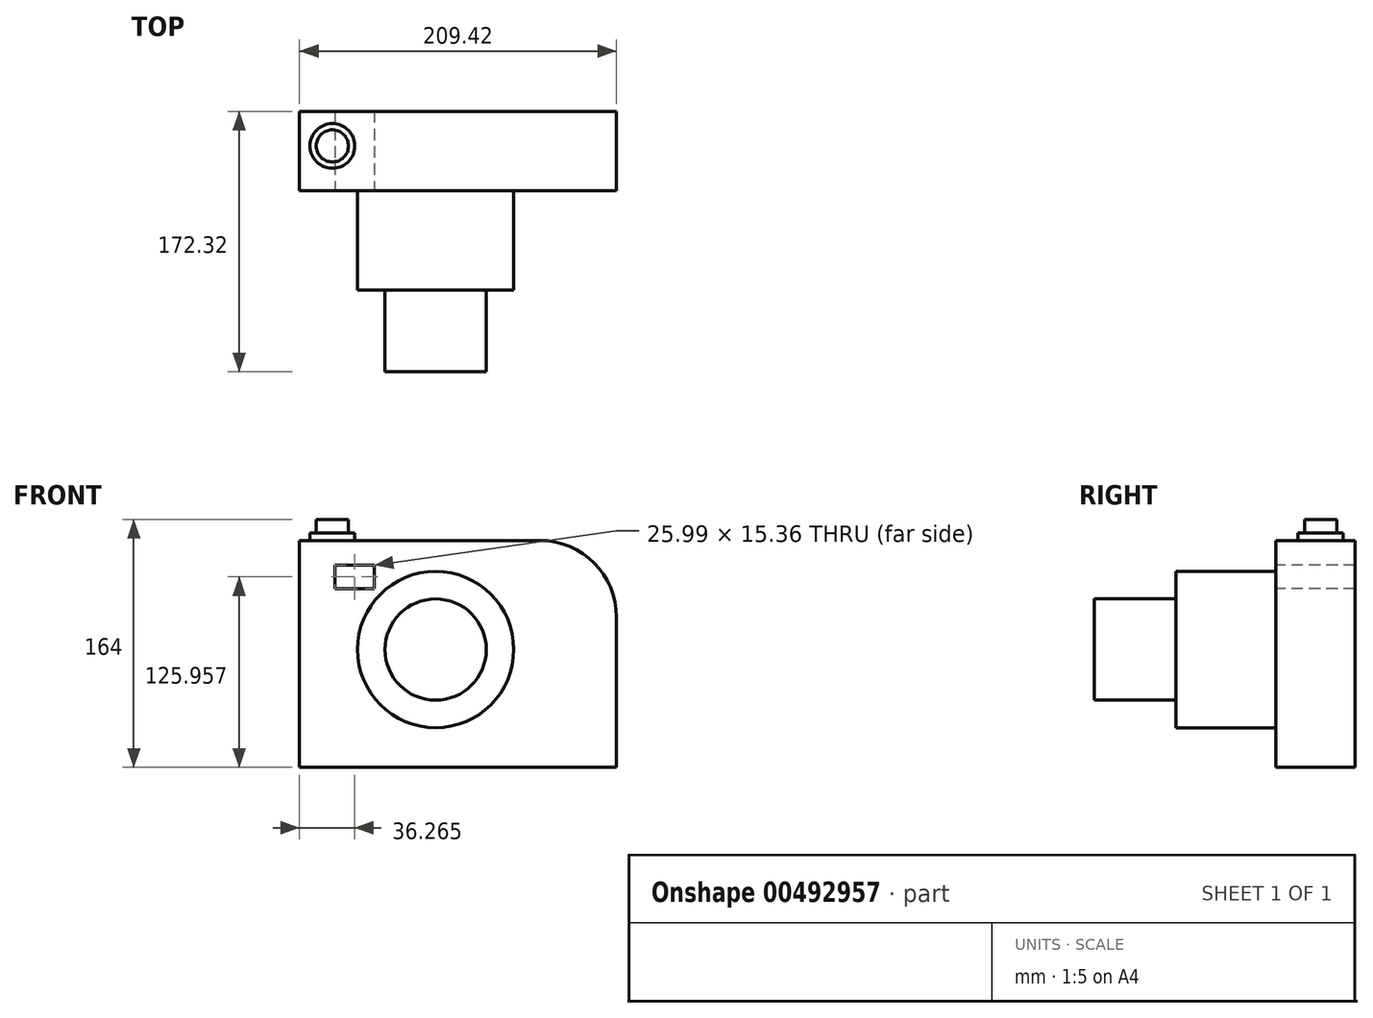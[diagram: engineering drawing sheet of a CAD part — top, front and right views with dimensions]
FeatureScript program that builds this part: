
annotation { "Feature Type Name" : "Feature", "Feature Type Description" : "" }
export const myFeature = defineFeature(function(context is Context, id is Id, definition is map)
    precondition{}
    {
        {
            var Q0;
            Q0=qCreatedBy(makeId("Top.planeOp"),FACE);
            var sketch = newSketch(context, id + "F0", { "sketchPlane" : qUnion([Q0])});
            skLineSegment(sketch, "E0.bottom", {"start": v(-159.83, -84.87) * mm, "end": v(49.6, -84.87) * mm});
            skLineSegment(sketch, "E0.top", {"start": v(-159.83, -32.55) * mm, "end": v(49.6, -32.55) * mm});
            skLineSegment(sketch, "E0.left", {"start": v(-159.83, -84.87) * mm, "end": v(-159.83, -32.55) * mm});
            skLineSegment(sketch, "E0.right", {"start": v(49.6, -84.87) * mm, "end": v(49.6, -32.55) * mm});
            skSolve(sketch);
        }
        {
            var Q0;
            Q0 = qSketchRegion(id + "F0", true);
            extrude(context, id + "F1", {"entities" : qUnion([Q0]), "depth" : 150 * mm});
        }
        {
            var Q0;
            Q0=makeQuery(id+"F1.opExtrude","CAP_EDGE",EDGE,{"disambiguationData":[OSD([sQuery(id+"F0.wireOp",EDGE,"E0.right")])],"isStart":false});
            fillet(context, id + "F2", {"entities" : qUnion([Q0]), "radius" : 50.7 * mm, "tangentPropagation" : true, "allowEdgeOverflow" : false});
        }
        {
            var Q0;
            Q0=makeQuery(id+"F1.opExtrude","SWEPT_FACE",FACE,{"disambiguationData":[OSD([sQuery(id+"F0.wireOp",EDGE,"E0.bottom")])]});
            var sketch = newSketch(context, id + "F3", { "sketchPlane" : qUnion([Q0])});
            skCircle(sketch, "E1", {"center": v(-69.93, 77.87) * mm, "radius": 51.66 * mm});
            skSolve(sketch);
        }
        {
            var Q0;
            Q0 = qSketchRegion(id + "F3", true);
            extrude(context, id + "F4", {"entities" : qUnion([Q0]), "operationType" : NewBodyOperationType.ADD, "depth" : 66 * mm});
        }
        {
            var Q0;
            Q0=makeQuery(id+"F4.opExtrude","CAP_FACE",FACE,{"disambiguationData":[OSD([sQuery(id+"F3.wireOp",EDGE,"E1")])],"isStart":false});
            var sketch = newSketch(context, id + "F5", { "sketchPlane" : qUnion([Q0])});
            skCircle(sketch, "E2", {"center": v(-69.93, 77.87) * mm, "radius": 33.47 * mm});
            skSolve(sketch);
        }
        {
            var Q0;
            Q0 = qSketchRegion(id + "F5", true);
            extrude(context, id + "F6", {"entities" : qUnion([Q0]), "operationType" : NewBodyOperationType.ADD, "depth" : 54 * mm});
        }
        {
            var Q0;
            Q0=makeQuery(id+"F1.opExtrude","CAP_FACE",FACE,{"disambiguationData":[OSD([sQuery(id+"F0.wireOp",EDGE,"E0.bottom"),sQuery(id+"F0.wireOp",EDGE,"E0.top"),sQuery(id+"F0.wireOp",EDGE,"E0.left"),sQuery(id+"F0.wireOp",EDGE,"E0.right")])],"isStart":false});
            var sketch = newSketch(context, id + "F7", { "sketchPlane" : qUnion([Q0])});
            skCircle(sketch, "E3", {"center": v(-138.17, -55.4) * mm, "radius": 14.8 * mm});
            skSolve(sketch);
        }
        {
            var Q0;
            Q0 = qSketchRegion(id + "F7", true);
            extrude(context, id + "F8", {"entities" : qUnion([Q0]), "operationType" : NewBodyOperationType.ADD, "depth" : 5 * mm});
        }
        {
            var Q0;
            Q0=makeQuery(id+"F8.opExtrude","CAP_FACE",FACE,{"disambiguationData":[OSD([sQuery(id+"F7.wireOp",EDGE,"E3")])],"isStart":false});
            var sketch = newSketch(context, id + "F9", { "sketchPlane" : qUnion([Q0])});
            skCircle(sketch, "E4", {"center": v(-138.17, -55.4) * mm, "radius": 10.62 * mm});
            skSolve(sketch);
        }
        {
            var Q0;
            Q0 = qSketchRegion(id + "F9", true);
            extrude(context, id + "F10", {"entities" : qUnion([Q0]), "operationType" : NewBodyOperationType.ADD, "depth" : 9 * mm});
        }
        {
            var Q0;
            Q0=makeQuery(id+"F1.opExtrude","SWEPT_FACE",FACE,{"disambiguationData":[OSD([sQuery(id+"F0.wireOp",EDGE,"E0.bottom")])]});
            var sketch = newSketch(context, id + "F11", { "sketchPlane" : qUnion([Q0])});
            skLineSegment(sketch, "E5.bottom", {"start": v(-152.36, 134.7) * mm, "end": v(-118.32, 134.7) * mm});
            skLineSegment(sketch, "E5.top", {"start": v(-152.36, 117.7) * mm, "end": v(-118.32, 117.7) * mm});
            skLineSegment(sketch, "E5.left", {"start": v(-152.36, 134.7) * mm, "end": v(-152.36, 117.7) * mm});
            skLineSegment(sketch, "E5.right", {"start": v(-118.32, 134.7) * mm, "end": v(-118.32, 117.7) * mm});
            skSolve(sketch);
        }
        {
            var Q0;
            Q0 = qSketchRegion(id + "F11", true);
            extrude(context, id + "F12", {"entities" : qUnion([Q0]), "operationType" : NewBodyOperationType.ADD, "oppositeDirection" : true, "depth" : 43 * mm});
        }
        {
            var Q0;
            Q0=makeQuery(id+"F1.opExtrude","SWEPT_FACE",FACE,{"disambiguationData":[OSD([sQuery(id+"F0.wireOp",EDGE,"E0.bottom")])]});
            var sketch = newSketch(context, id + "F13", { "sketchPlane" : qUnion([Q0])});
            skLineSegment(sketch, "E6.bottom", {"start": v(-136.56, 133.64) * mm, "end": v(-110.57, 133.64) * mm});
            skLineSegment(sketch, "E6.top", {"start": v(-136.56, 118.28) * mm, "end": v(-110.57, 118.28) * mm});
            skLineSegment(sketch, "E6.left", {"start": v(-136.56, 133.64) * mm, "end": v(-136.56, 118.28) * mm});
            skLineSegment(sketch, "E6.right", {"start": v(-110.57, 133.64) * mm, "end": v(-110.57, 118.28) * mm});
            skSolve(sketch);
        }
        {
            var Q0;
            Q0 = qSketchRegion(id + "F13", true);
            extrude(context, id + "F14", {"entities" : qUnion([Q0]), "operationType" : NewBodyOperationType.REMOVE, "oppositeDirection" : true, "depth" : 77 * mm});
        }
    });
